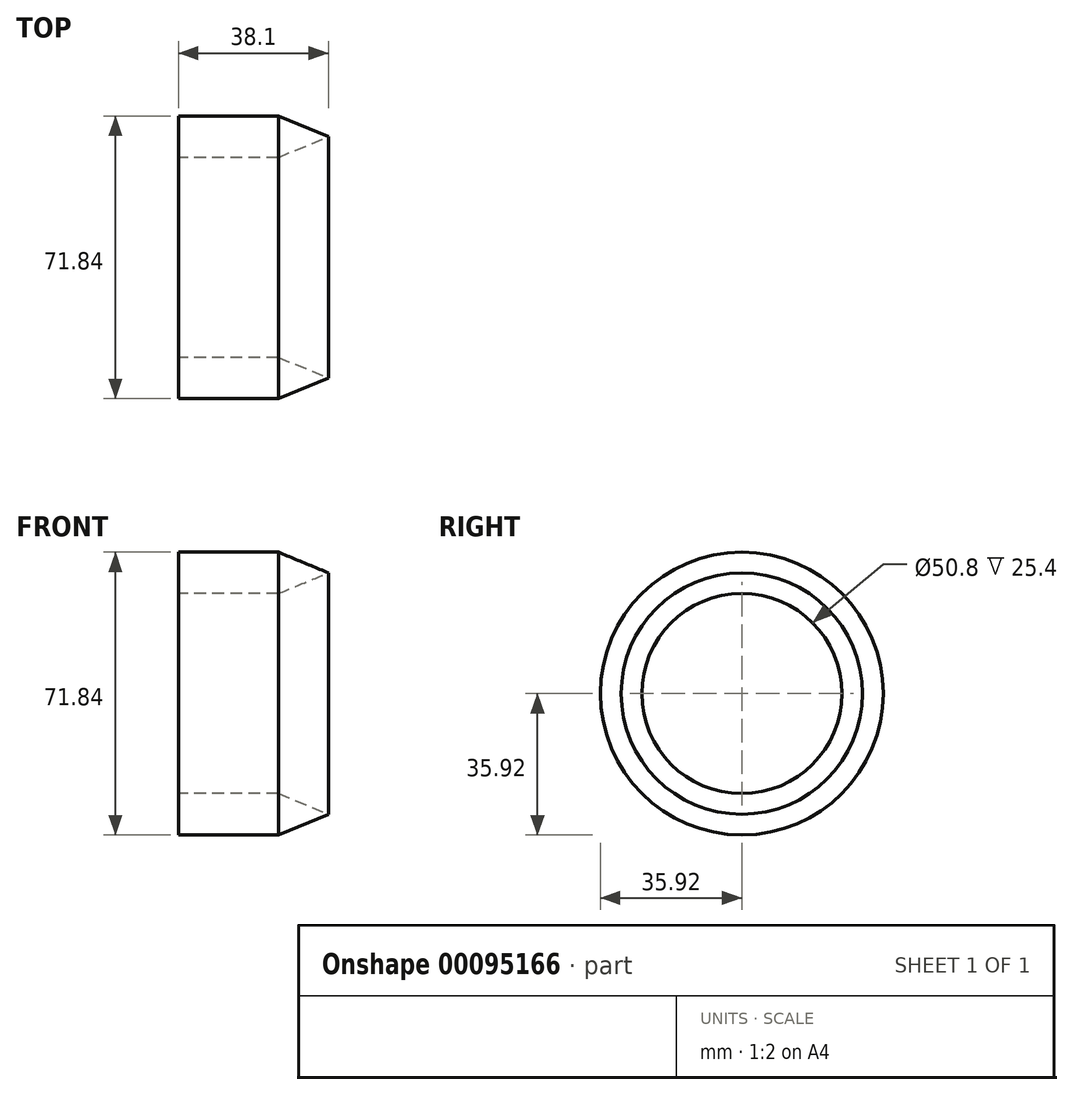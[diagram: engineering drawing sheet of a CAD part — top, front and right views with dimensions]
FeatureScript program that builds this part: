
annotation { "Feature Type Name" : "Feature", "Feature Type Description" : "" }
export const myFeature = defineFeature(function(context is Context, id is Id, definition is map)
    precondition{}
    {
        {
            var Q0;
            Q0=qCreatedBy(makeId("Front.planeOp"),FACE);
            var sketch = newSketch(context, id + "F0", { "sketchPlane" : qUnion([Q0])});
            skLineSegment(sketch, "E0", {"start": v(0, -25.4) * mm, "end": v(0, -35.92) * mm});
            skLineSegment(sketch, "E1", {"start": v(25.4, -35.92) * mm, "end": v(0, -35.92) * mm});
            skLineSegment(sketch, "E2", {"start": v(25.4, -35.92) * mm, "end": v(38.1, -30.66) * mm});
            skLineSegment(sketch, "E3", {"start": v(38.1, -30.66) * mm, "end": v(25.4, -25.4) * mm});
            skLineSegment(sketch, "E4", {"start": v(0, -25.4) * mm, "end": v(25.4, -25.4) * mm});
            skSolve(sketch);
        }
        {
            var Q0;
            Q0=qCreatedBy(makeId("Front.planeOp"),FACE);
            var sketch = newSketch(context, id + "F1", { "sketchPlane" : qUnion([Q0])});
            skLineSegment(sketch, "E5", {"start": v(0, 0) * mm, "end": v(64.55, 0) * mm, "construction": true});
            skSolve(sketch);
        }
        {
            var Q0;
            Q0 = qSketchRegion(id + "F0", true);
            var Q1;
            Q1=sQuery(id+"F1.wireOp",EDGE,"E5");
            revolve(context, id + "F2", {"entities" : qUnion([Q0]), "axis" : qUnion([Q1]), "revolveType" : RevolveType.FULL});
        }
    });
